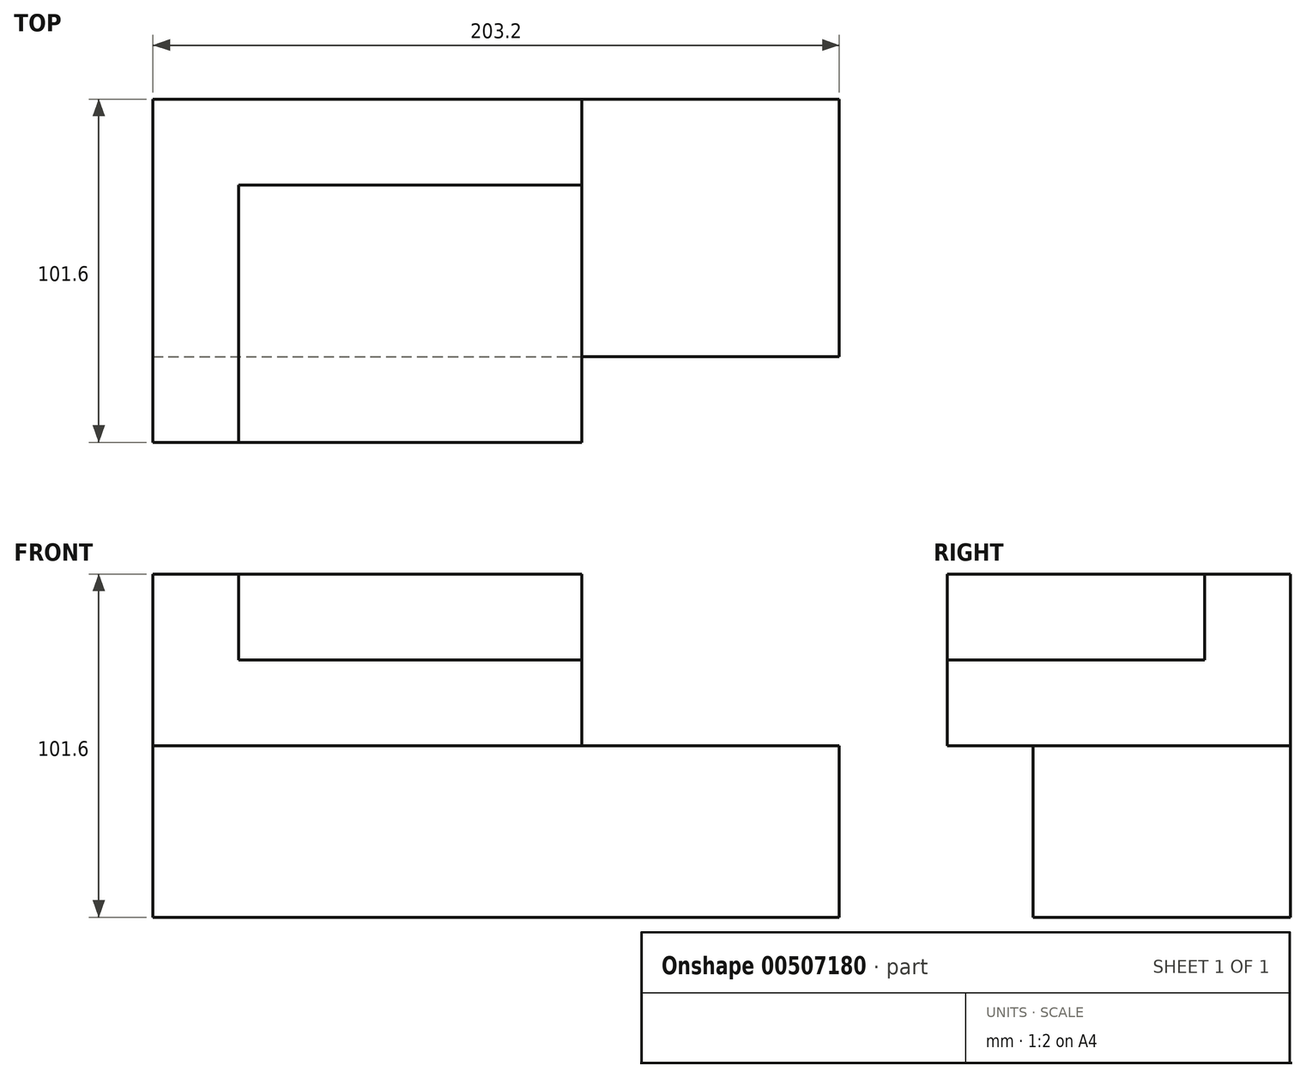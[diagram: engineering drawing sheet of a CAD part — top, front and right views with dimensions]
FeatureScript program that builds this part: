
annotation { "Feature Type Name" : "Feature", "Feature Type Description" : "" }
export const myFeature = defineFeature(function(context is Context, id is Id, definition is map)
    precondition{}
    {
        {
            var Q0;
            Q0=qCreatedBy(makeId("Top.planeOp"),FACE);
            var sketch = newSketch(context, id + "F0", { "sketchPlane" : qUnion([Q0])});
            skLineSegment(sketch, "E0.bottom", {"start": v(0, 0) * mm, "end": v(203.2, 0) * mm});
            skLineSegment(sketch, "E0.top", {"start": v(0, -76.2) * mm, "end": v(203.2, -76.2) * mm});
            skLineSegment(sketch, "E0.left", {"start": v(0, 0) * mm, "end": v(0, -76.2) * mm});
            skLineSegment(sketch, "E0.right", {"start": v(203.2, 0) * mm, "end": v(203.2, -76.2) * mm});
            skSolve(sketch);
        }
        {
            var Q0;
            Q0=makeQuery(id+"F0.imprint","IMPRINT",FACE,{"disambiguationData":[TD([[makeQuery(id+"F0.imprint","IMPRINT",EDGE,{"derivedFrom":sQuery(id+"F0.wireOp",EDGE,"E0.bottom")}),-1.0]])]});
            extrude(context, id + "F1", {"entities" : qUnion([Q0]), "depth" : 50.8 * mm});
        }
        {
            var Q0;
            Q0=makeQuery(id+"F1.opExtrude","CAP_FACE",FACE,{"disambiguationData":[OSD([sQuery(id+"F0.wireOp",EDGE,"E0.bottom"),sQuery(id+"F0.wireOp",EDGE,"E0.top"),sQuery(id+"F0.wireOp",EDGE,"E0.left"),sQuery(id+"F0.wireOp",EDGE,"E0.right")])],"isStart":false});
            var sketch = newSketch(context, id + "F2", { "sketchPlane" : qUnion([Q0])});
            skLineSegment(sketch, "E1.bottom", {"start": v(0, 0) * mm, "end": v(127, 0) * mm});
            skLineSegment(sketch, "E1.top", {"start": v(0, -101.6) * mm, "end": v(127, -101.6) * mm});
            skLineSegment(sketch, "E1.left", {"start": v(0, 0) * mm, "end": v(0, -101.6) * mm});
            skLineSegment(sketch, "E1.right", {"start": v(127, 0) * mm, "end": v(127, -101.6) * mm});
            skSolve(sketch);
        }
        {
            var Q0;
            {var subQ0=sQuery(id+"F2.wireOp",EDGE,"E1.top");Q0=makeQuery(id+"F2.imprint","IMPRINT",FACE,{"disambiguationData":[TD([[makeQuery(id+"F2.imprint","IMPRINT",EDGE,{"derivedFrom":subQ0}),1.0]])]});}
            var Q1;
            {var subQ0=sQuery(id+"F2.wireOp",EDGE,"E1.bottom");Q1=makeQuery(id+"F2.imprint","IMPRINT",FACE,{"disambiguationData":[TD([[makeQuery(id+"F2.imprint","IMPRINT",EDGE,{"derivedFrom":subQ0}),-1.0]])]});}
            extrude(context, id + "F3", {"entities" : qUnion([Q0, Q1]), "operationType" : NewBodyOperationType.ADD, "depth" : 25.4 * mm});
        }
        {
            var Q0;
            Q0=makeQuery(id+"F3.opExtrude","CAP_FACE",FACE,{"disambiguationData":[OSD([sQuery(id+"F2.wireOp",EDGE,"E1.bottom"),sQuery(id+"F2.wireOp",EDGE,"E1.top"),sQuery(id+"F2.wireOp",EDGE,"E1.left"),sQuery(id+"F2.wireOp",EDGE,"E1.right")])],"isStart":false});
            var sketch = newSketch(context, id + "F4", { "sketchPlane" : qUnion([Q0])});
            skLineSegment(sketch, "E2", {"start": v(0, -101.6) * mm, "end": v(25.4, -101.6) * mm});
            skLineSegment(sketch, "E3", {"start": v(25.4, -101.6) * mm, "end": v(25.4, -25.4) * mm});
            skLineSegment(sketch, "E4", {"start": v(25.4, -25.4) * mm, "end": v(127, -25.4) * mm});
            skLineSegment(sketch, "E5", {"start": v(127, -25.4) * mm, "end": v(127, 0) * mm});
            skLineSegment(sketch, "E6", {"start": v(127, 0) * mm, "end": v(0, 0) * mm});
            skLineSegment(sketch, "E7", {"start": v(0, 0) * mm, "end": v(0, -101.6) * mm});
            skSolve(sketch);
        }
        {
            var Q0;
            Q0=makeQuery(id+"F4.imprint","IMPRINT",FACE,{"disambiguationData":[TD([[makeQuery(id+"F4.imprint","IMPRINT",EDGE,{"derivedFrom":sQuery(id+"F4.wireOp",EDGE,"E2")}),1.0]])]});
            extrude(context, id + "F5", {"entities" : qUnion([Q0]), "operationType" : NewBodyOperationType.ADD, "depth" : 25.4 * mm});
        }
    });
